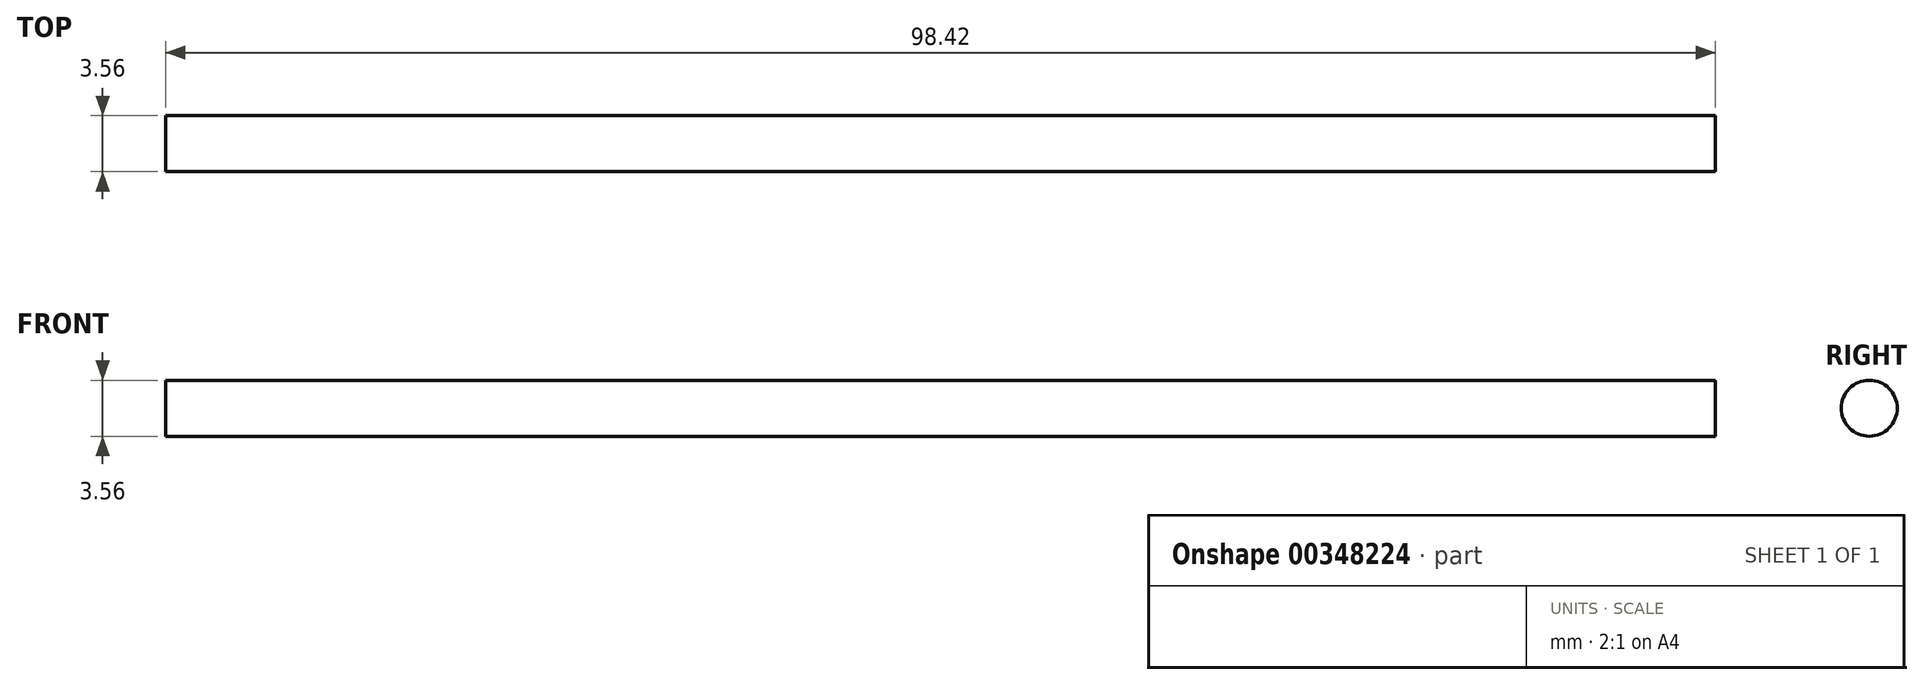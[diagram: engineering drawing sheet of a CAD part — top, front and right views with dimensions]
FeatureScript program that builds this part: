
annotation { "Feature Type Name" : "Feature", "Feature Type Description" : "" }
export const myFeature = defineFeature(function(context is Context, id is Id, definition is map)
    precondition{}
    {
        {
            var Q0;
            Q0=qCreatedBy(makeId("Right.planeOp"),FACE);
            var sketch = newSketch(context, id + "F0", { "sketchPlane" : qUnion([Q0])});
            skCircle(sketch, "E0", {"center": v(0, 0) * mm, "radius": 1.78 * mm});
            skSolve(sketch);
        }
        {
            var Q0;
            Q0=qSketchRegion(id+"F0",true);
            extrude(context, id + "F1", {"entities" : qUnion([Q0]), "endBound" : BoundingType.SYMMETRIC, "depth" : 98.42 * mm});
        }
    });
